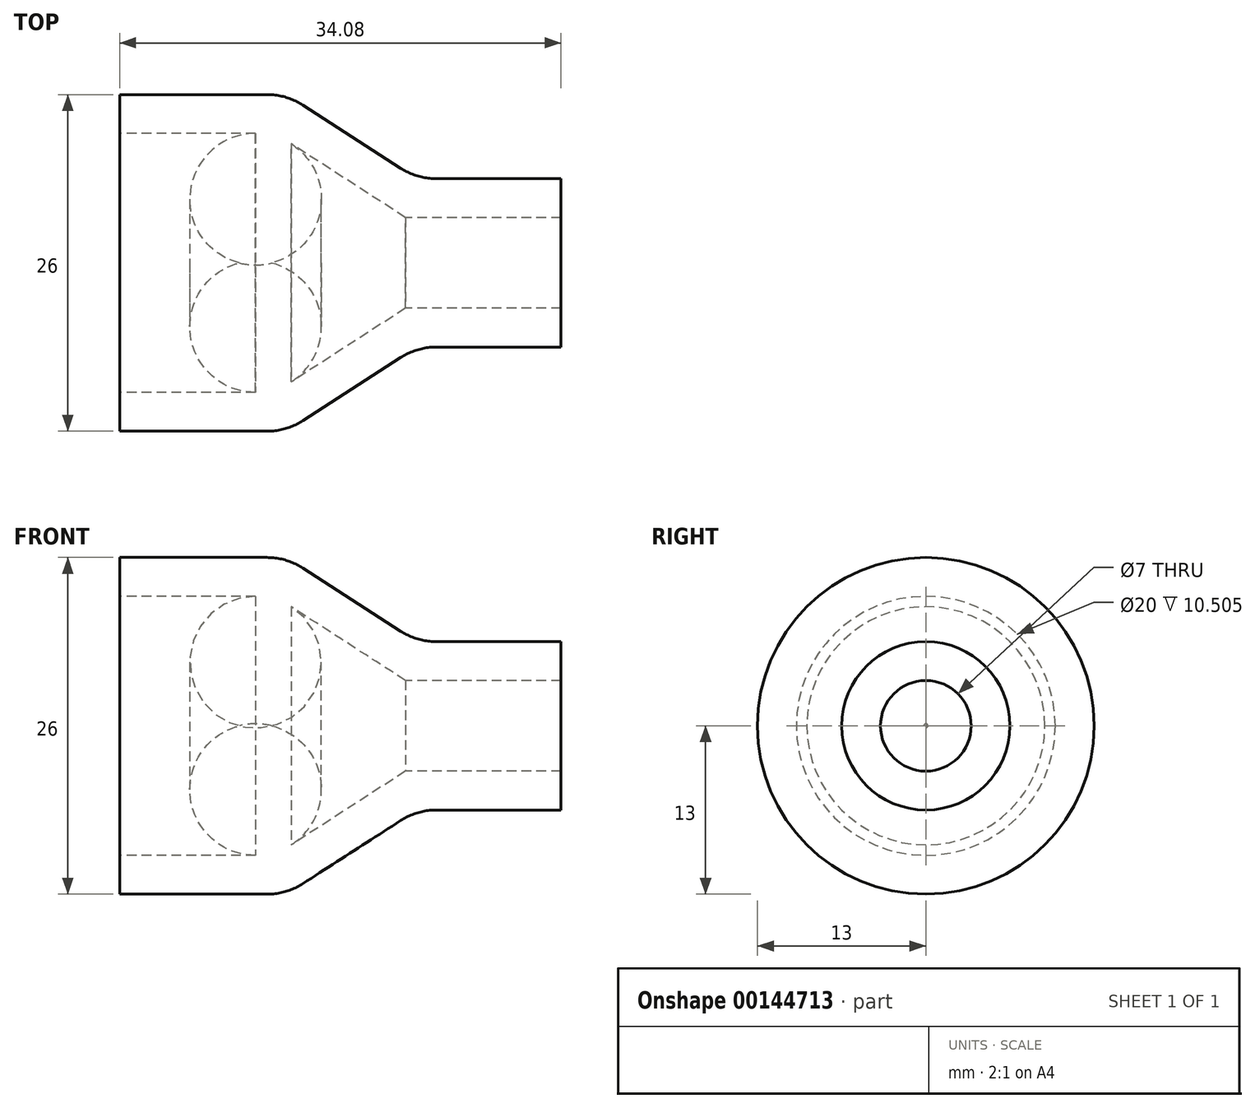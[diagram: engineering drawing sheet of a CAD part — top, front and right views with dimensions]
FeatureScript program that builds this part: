
annotation { "Feature Type Name" : "Feature", "Feature Type Description" : "" }
export const myFeature = defineFeature(function(context is Context, id is Id, definition is map)
    precondition{}
    {
        {
            var Q0;
            Q0=qCreatedBy(makeId("Front.planeOp"),FACE);
            var sketch = newSketch(context, id + "F0", { "sketchPlane" : qUnion([Q0])});
            skLineSegment(sketch, "E0", {"start": v(-12.7, 0) * mm, "end": v(12.7, 0) * mm, "construction": true});
            skLineSegment(sketch, "E1", {"start": v(3.32, 3.5) * mm, "end": v(15.32, 3.5) * mm});
            skLineSegment(sketch, "E2", {"start": v(3.32, 3.5) * mm, "end": v(-6.76, 10) * mm});
            skLineSegment(sketch, "E3", {"start": v(-6.76, 10) * mm, "end": v(-18.76, 10) * mm});
            skPoint(sketch, "E4", {"position": v(0, 5.64) * mm});
            skLineSegment(sketch, "E5.0", {"start": v(-5.88, 13) * mm, "end": v(-18.76, 13) * mm});
            skLineSegment(sketch, "E5.1", {"start": v(4.2, 6.5) * mm, "end": v(-5.88, 13) * mm});
            skLineSegment(sketch, "E5.2", {"start": v(4.2, 6.5) * mm, "end": v(15.32, 6.5) * mm});
            skLineSegment(sketch, "E6", {"start": v(15.32, 6.5) * mm, "end": v(15.32, 3.5) * mm});
            skLineSegment(sketch, "E7", {"start": v(-18.76, 13) * mm, "end": v(-18.76, 10) * mm});
            skSolve(sketch);
        }
        {
            var Q0;
            Q0 = qSketchRegion(id + "F0", true);
            var Q1;
            Q1=sQuery(id+"F0.wireOp",EDGE,"E0");
            revolve(context, id + "F1", {"entities" : qUnion([Q0]), "axis" : qUnion([Q1]), "revolveType" : RevolveType.FULL});
        }
        {
            var Q0;
            Q0=makeQuery(id+"F1.opRevolve","SWEPT_EDGE",EDGE,{"disambiguationData":[OSD([sQuery(id+"F0.wireOp",EDGE,"E5.1"),sQuery(id+"F0.wireOp",EDGE,"E5.2")])]});
            var Q1;
            Q1=makeQuery(id+"F1.opRevolve","SWEPT_EDGE",EDGE,{"disambiguationData":[OSD([sQuery(id+"F0.wireOp",EDGE,"E5.0"),sQuery(id+"F0.wireOp",EDGE,"E5.1")])]});
            var Q2;
            Q2=makeQuery(id+"F1.opRevolve","SWEPT_EDGE",EDGE,{"disambiguationData":[OSD([sQuery(id+"F0.wireOp",EDGE,"E2"),sQuery(id+"F0.wireOp",EDGE,"E3")])]});
            fillet(context, id + "F2", {"entities" : qUnion([Q0, Q1, Q2]), "radius" : 5.08 * mm, "tangentPropagation" : true, "allowEdgeOverflow" : false});
        }
    });
